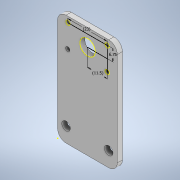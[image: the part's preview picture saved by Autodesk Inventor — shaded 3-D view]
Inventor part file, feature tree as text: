
AUTODESK INVENTOR PART (.ipt)
format: ipt  version: 2021 (Build 250183000, 183)  size: 128,000 bytes
history: native  units: mm
features: sketch x2, other x1, extrude x1
ambient origin geometry x8: Origin, YZ Plane, XZ Plane, XY Plane, X Axis, Y Axis, Z Axis, Center Point
bodies: Body1 (feature_tree)
feature tree (4):
  other  "Sólido1"
  extrude  "Extrusión1"  Depth=3.0mm
  sketch  "Boceto2"  dims[d21=6.75mm d22=11.5mm]
  sketch  "Boceto1"  dims[d18=3.0mm d19=0.0mm d20=23.0mm]
